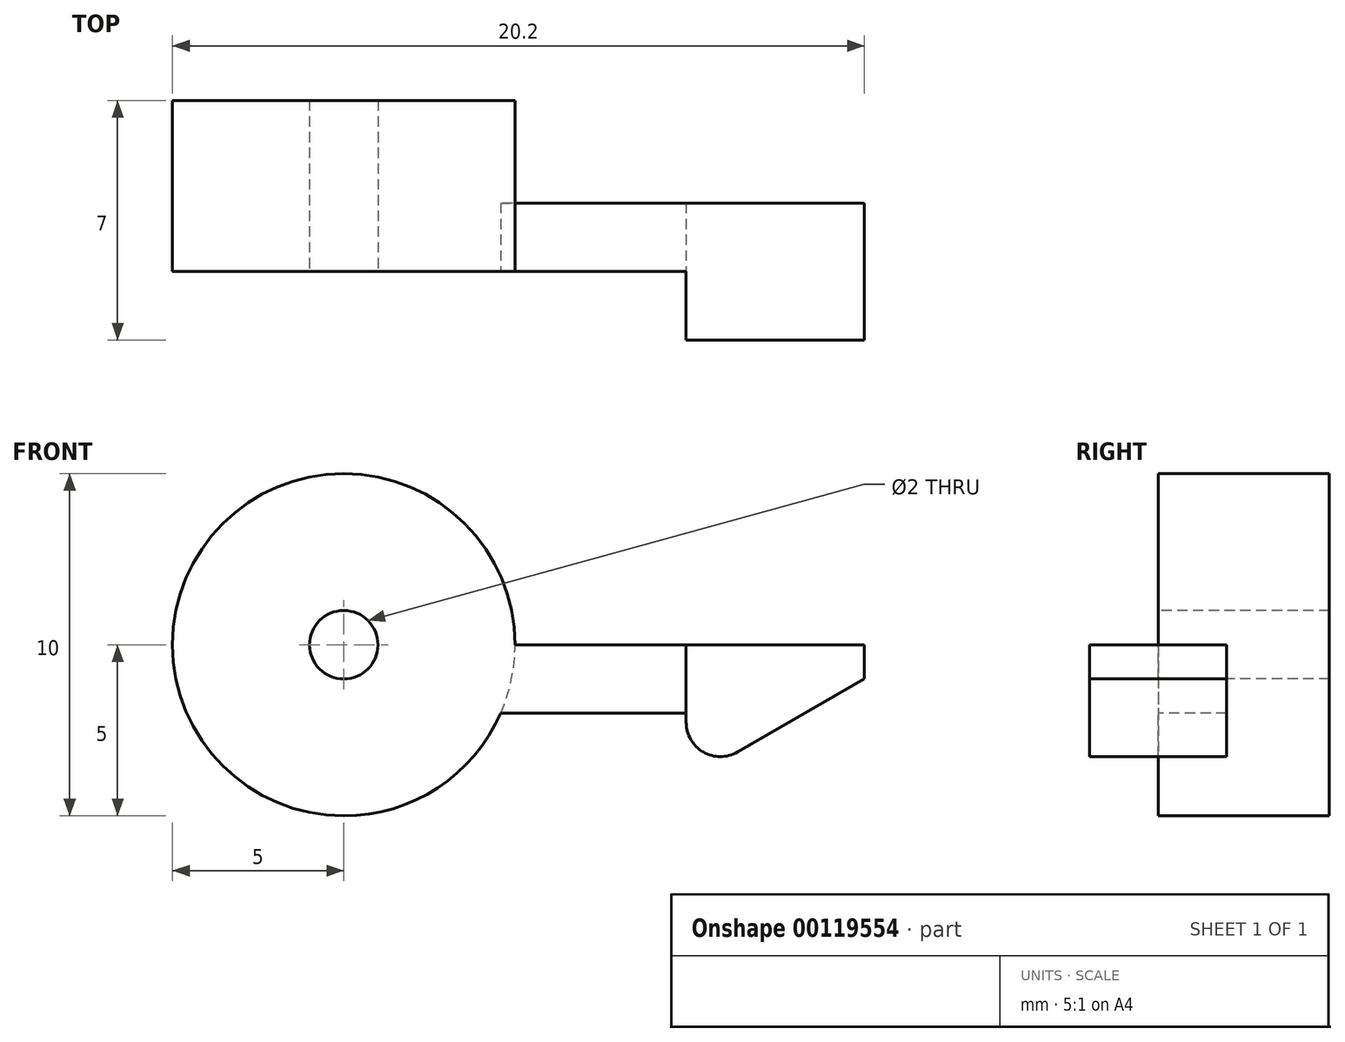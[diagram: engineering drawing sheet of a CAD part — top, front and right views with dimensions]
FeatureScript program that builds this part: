
annotation { "Feature Type Name" : "Feature", "Feature Type Description" : "" }
export const myFeature = defineFeature(function(context is Context, id is Id, definition is map)
    precondition{}
    {
        {
            var Q0;
            Q0=qCreatedBy(makeId("Front.planeOp"),FACE);
            var sketch = newSketch(context, id + "F0", { "sketchPlane" : qUnion([Q0])});
            skCircle(sketch, "E0", {"center": v(0, 0) * mm, "radius": 5 * mm});
            skLineSegment(sketch, "E1", {"start": v(5, 0) * mm, "end": v(10, 0) * mm});
            skLineSegment(sketch, "E2", {"start": v(15.2, 0) * mm, "end": v(10, 0) * mm});
            skLineSegment(sketch, "E3.MirrorCS", {"start": v(10, -2) * mm, "end": v(4.58, -2) * mm});
            skLineSegment(sketch, "E4.MirrorCS", {"start": v(10, -2) * mm, "end": v(10, -4) * mm});
            skLineSegment(sketch, "E5.MirrorCS", {"start": v(10, -4) * mm, "end": v(15.2, -1) * mm});
            skLineSegment(sketch, "E6.MirrorCS", {"start": v(15.2, -1) * mm, "end": v(15.2, 0) * mm});
            skLineSegment(sketch, "E7.MirrorCS", {"start": v(10, 0) * mm, "end": v(10, -2) * mm});
            skSolve(sketch);
        }
        {
            var Q0;
            {var subQ0=sQuery(id+"F0.wireOp",EDGE,"E0");var subQ1=makeQuery(id+"F0.imprint","INTERSECT",VERTEX,{"derivedFrom":[subQ0,sQuery(id+"F0.wireOp",EDGE,"E1")]});Q0=makeQuery(id+"F0.imprint","IMPRINT",FACE,{"disambiguationData":[TD([[makeQuery(id+"F0.imprint","IMPRINT",EDGE,{"disambiguationData":[TD([[subQ1,-1.0]])],"derivedFrom":subQ0}),1.0]])]});}
            extrude(context, id + "F1", {"entities" : qUnion([Q0]), "oppositeDirection" : true, "depth" : 5 * mm});
        }
        {
            var Q0;
            Q0=sQuery(id+"F0.wireOp",VERTEX,"E0.center");
            var Q1;
            Q1=makeQuery(id+"F1.opExtrude","SWEPT_BODY",BODY,{"disambiguationData":[OSD([sQuery(id+"F0.wireOp",EDGE,"E0")])]});
            hole(context, id + "F2", {"style" : HoleStyle.SIMPLE, "endStyle" : HoleEndStyle.THROUGH, "holeDiameter" : 2 * mm, "locations" : qUnion([Q0]), "scope" : qUnion([Q1]), "isTappedThrough" : true});
        }
        {
            var Q0;
            {var subQ0=sQuery(id+"F0.wireOp",EDGE,"E3.MirrorCS");Q0=makeQuery(id+"F0.imprint","IMPRINT",FACE,{"disambiguationData":[TD([[makeQuery(id+"F0.imprint","IMPRINT",EDGE,{"derivedFrom":subQ0}),-1.0]])]});}
            extrude(context, id + "F3", {"entities" : qUnion([Q0]), "operationType" : NewBodyOperationType.ADD, "oppositeDirection" : true, "depth" : 2 * mm});
        }
        {
            var Q0;
            Q0=makeQuery(id+"F0.imprint","IMPRINT",FACE,{"disambiguationData":[TD([[makeQuery(id+"F0.imprint","IMPRINT",EDGE,{"derivedFrom":sQuery(id+"F0.wireOp",EDGE,"E2")}),1.0]])]});
            extrude(context, id + "F4", {"entities" : qUnion([Q0]), "operationType" : NewBodyOperationType.ADD, "endBound" : BoundingType.SYMMETRIC, "oppositeDirection" : true, "depth" : 4 * mm});
        }
        {
            var Q0;
            Q0=makeQuery(id+"F4.opExtrude","SWEPT_EDGE",EDGE,{"disambiguationData":[OSD([sQuery(id+"F0.wireOp",EDGE,"E4.MirrorCS"),sQuery(id+"F0.wireOp",EDGE,"E5.MirrorCS")])]});
            fillet(context, id + "F5", {"entities" : qUnion([Q0]), "radius" : 1 * mm, "tangentPropagation" : true, "allowEdgeOverflow" : false});
        }
    });
